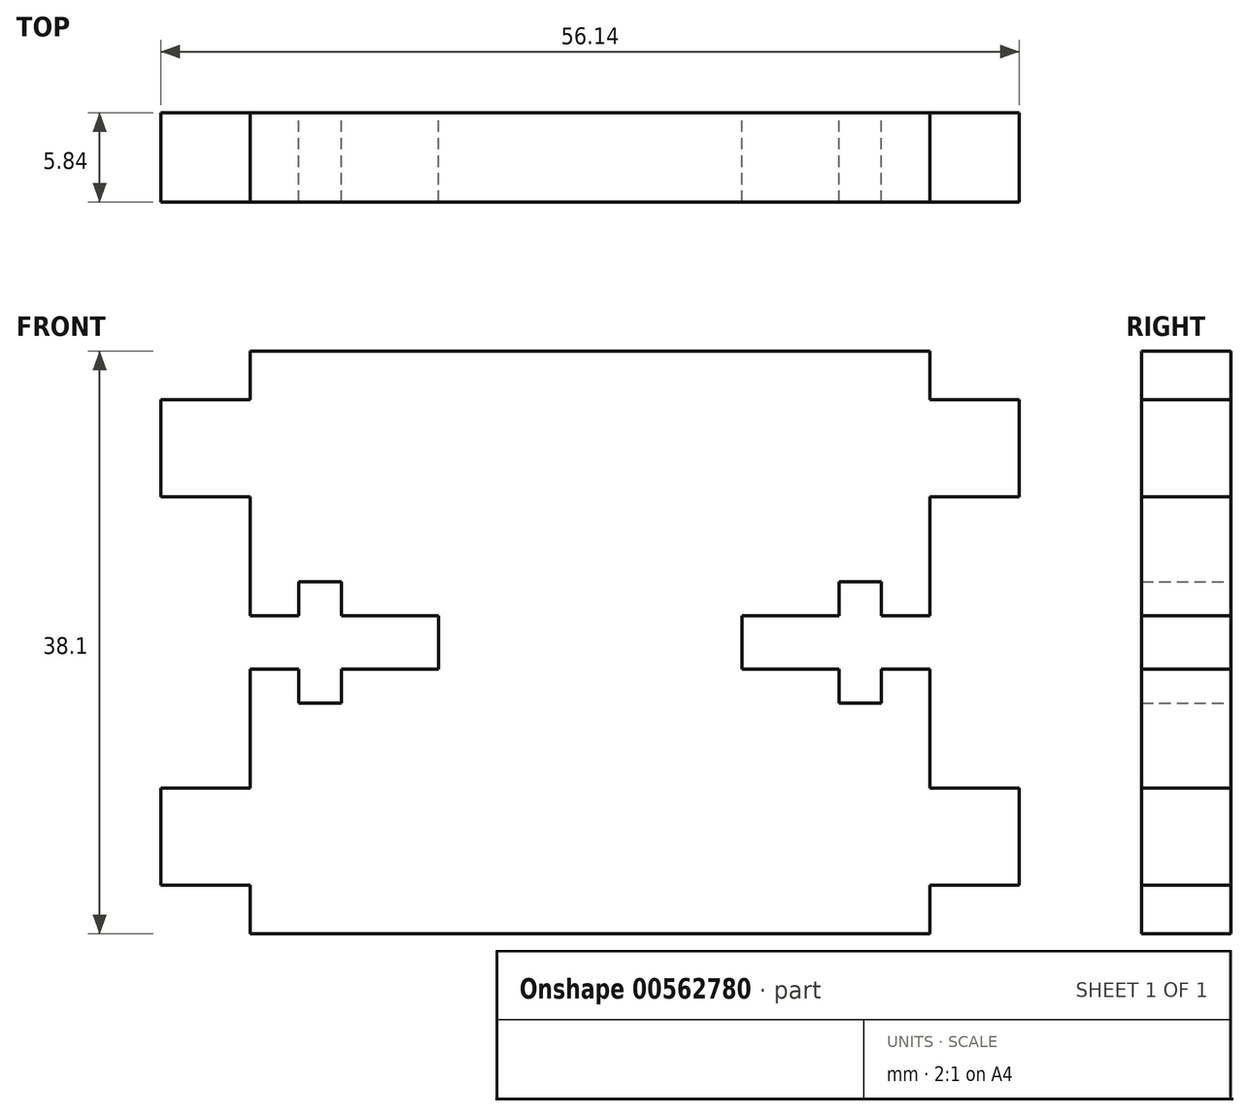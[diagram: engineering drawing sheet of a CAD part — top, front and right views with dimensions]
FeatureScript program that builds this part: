
annotation { "Feature Type Name" : "Feature", "Feature Type Description" : "" }
export const myFeature = defineFeature(function(context is Context, id is Id, definition is map)
    precondition{}
    {
        {
            var Q0;
            Q0=qCreatedBy(makeId("Front.planeOp"),FACE);
            var sketch = newSketch(context, id + "F0", { "sketchPlane" : qUnion([Q0])});
            skLineSegment(sketch, "E0.bottom", {"start": v(-22.22, 19.05) * mm, "end": v(22.23, 19.05) * mm});
            skLineSegment(sketch, "E0.top", {"start": v(-22.23, -19.05) * mm, "end": v(22.23, -19.05) * mm});
            skLineSegment(sketch, "E0.left", {"start": v(-22.22, 19.05) * mm, "end": v(-22.22, 15.87) * mm});
            skLineSegment(sketch, "E0.right", {"start": v(22.23, 19.05) * mm, "end": v(22.23, 15.87) * mm});
            skPoint(sketch, "E0.middle", {"position": v(0, 0) * mm});
            skLineSegment(sketch, "E1.bottom", {"start": v(-22.23, 15.87) * mm, "end": v(-28.07, 15.87) * mm});
            skLineSegment(sketch, "E1.top", {"start": v(-22.23, 9.52) * mm, "end": v(-28.07, 9.52) * mm});
            skLineSegment(sketch, "E1.right", {"start": v(-28.07, 15.87) * mm, "end": v(-28.07, 9.52) * mm});
            skPoint(sketch, "E1.middle", {"position": v(-25.15, 12.7) * mm});
            skLineSegment(sketch, "E2.trimOffspring", {"start": v(-22.23, 9.52) * mm, "end": v(-22.23, 1.75) * mm});
            skLineSegment(sketch, "E3.MirrorCS", {"start": v(-22.23, -15.87) * mm, "end": v(-28.07, -15.87) * mm});
            skLineSegment(sketch, "E4.MirrorCS", {"start": v(-28.07, -15.87) * mm, "end": v(-28.07, -9.52) * mm});
            skLineSegment(sketch, "E5.MirrorCS", {"start": v(-22.23, -9.52) * mm, "end": v(-28.07, -9.52) * mm});
            skPoint(sketch, "E6.MirrorP", {"position": v(-25.15, -12.7) * mm});
            skLineSegment(sketch, "E7.trimOffspring", {"start": v(-22.23, -15.87) * mm, "end": v(-22.23, -19.05) * mm});
            skLineSegment(sketch, "E8.MirrorCS", {"start": v(22.23, 15.87) * mm, "end": v(28.07, 15.87) * mm});
            skLineSegment(sketch, "E9.MirrorCS", {"start": v(22.23, 9.52) * mm, "end": v(28.07, 9.52) * mm});
            skPoint(sketch, "E10.MirrorP", {"position": v(25.15, -12.7) * mm});
            skLineSegment(sketch, "E11.MirrorCS", {"start": v(28.07, 15.87) * mm, "end": v(28.07, 9.52) * mm});
            skPoint(sketch, "E12.MirrorP", {"position": v(25.15, 12.7) * mm});
            skLineSegment(sketch, "E13.MirrorCS", {"start": v(22.23, -9.52) * mm, "end": v(28.07, -9.52) * mm});
            skLineSegment(sketch, "E14.MirrorCS", {"start": v(28.07, -15.87) * mm, "end": v(28.07, -9.52) * mm});
            skLineSegment(sketch, "E15.MirrorCS", {"start": v(22.23, -15.87) * mm, "end": v(28.07, -15.87) * mm});
            skLineSegment(sketch, "E16.MirrorCS", {"start": v(22.23, 9.52) * mm, "end": v(22.23, 1.75) * mm});
            skLineSegment(sketch, "E17.trimOffspring", {"start": v(22.23, -15.87) * mm, "end": v(22.23, -19.05) * mm});
            skLineSegment(sketch, "E18.bottom", {"start": v(-22.23, 1.75) * mm, "end": v(-19.05, 1.75) * mm});
            skLineSegment(sketch, "E18.top", {"start": v(-22.22, -1.75) * mm, "end": v(-19.05, -1.75) * mm});
            skPoint(sketch, "E18.middle", {"position": v(-20.64, 0) * mm});
            skLineSegment(sketch, "E19.bottom", {"start": v(-19.05, 3.97) * mm, "end": v(-16.27, 3.97) * mm});
            skLineSegment(sketch, "E19.top", {"start": v(-19.05, -3.97) * mm, "end": v(-16.27, -3.97) * mm});
            skLineSegment(sketch, "E19.left", {"start": v(-19.05, 3.97) * mm, "end": v(-19.05, 1.75) * mm});
            skLineSegment(sketch, "E19.right", {"start": v(-16.27, 3.97) * mm, "end": v(-16.27, 1.75) * mm});
            skPoint(sketch, "E19.middle", {"position": v(-17.66, 0) * mm});
            skLineSegment(sketch, "E20.bottom", {"start": v(-16.27, 1.75) * mm, "end": v(-9.92, 1.75) * mm});
            skLineSegment(sketch, "E20.top", {"start": v(-16.27, -1.75) * mm, "end": v(-9.92, -1.75) * mm});
            skLineSegment(sketch, "E20.right", {"start": v(-9.92, 1.75) * mm, "end": v(-9.92, -1.75) * mm});
            skPoint(sketch, "E20.middle", {"position": v(-13.1, 0) * mm});
            skLineSegment(sketch, "E21.trimOffspring", {"start": v(-19.05, -1.75) * mm, "end": v(-19.05, -3.97) * mm});
            skLineSegment(sketch, "E22.trimOffspring", {"start": v(-16.27, -1.75) * mm, "end": v(-16.27, -3.97) * mm});
            skLineSegment(sketch, "E23.trimOffspring", {"start": v(-22.23, -1.75) * mm, "end": v(-22.23, -9.52) * mm});
            skPoint(sketch, "E24.MirrorP", {"position": v(17.66, 0) * mm});
            skLineSegment(sketch, "E25.MirrorCS", {"start": v(19.05, -1.75) * mm, "end": v(19.05, -3.97) * mm});
            skLineSegment(sketch, "E26.MirrorCS", {"start": v(19.05, 3.97) * mm, "end": v(19.05, 1.75) * mm});
            skLineSegment(sketch, "E27.MirrorCS", {"start": v(22.22, -1.75) * mm, "end": v(19.05, -1.75) * mm});
            skLineSegment(sketch, "E28.MirrorCS", {"start": v(22.23, 1.75) * mm, "end": v(19.05, 1.75) * mm});
            skLineSegment(sketch, "E29.MirrorCS", {"start": v(19.05, -3.97) * mm, "end": v(16.27, -3.97) * mm});
            skLineSegment(sketch, "E30.MirrorCS", {"start": v(16.27, -1.75) * mm, "end": v(16.27, -3.97) * mm});
            skLineSegment(sketch, "E31.MirrorCS", {"start": v(19.05, 3.97) * mm, "end": v(16.27, 3.97) * mm});
            skLineSegment(sketch, "E32.MirrorCS", {"start": v(16.27, 1.75) * mm, "end": v(9.92, 1.75) * mm});
            skPoint(sketch, "E33.MirrorP", {"position": v(20.64, 0) * mm});
            skLineSegment(sketch, "E34.MirrorCS", {"start": v(22.23, -1.75) * mm, "end": v(22.23, -9.52) * mm});
            skPoint(sketch, "E35.MirrorP", {"position": v(13.1, 0) * mm});
            skLineSegment(sketch, "E36.MirrorCS", {"start": v(9.92, 1.75) * mm, "end": v(9.92, -1.75) * mm});
            skLineSegment(sketch, "E37.MirrorCS", {"start": v(16.27, 3.97) * mm, "end": v(16.27, 1.75) * mm});
            skLineSegment(sketch, "E38.MirrorCS", {"start": v(16.27, -1.75) * mm, "end": v(9.92, -1.75) * mm});
            skSolve(sketch);
        }
        {
            var Q0;
            Q0 = qSketchRegion(id + "F0", true);
            extrude(context, id + "F1", {"entities" : qUnion([Q0]), "depth" : 5.84 * mm, "offsetDistance" : 25.4 * mm});
        }
    });
